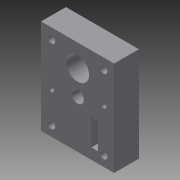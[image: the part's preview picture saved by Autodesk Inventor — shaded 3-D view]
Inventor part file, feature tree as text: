
AUTODESK INVENTOR PART (.ipt)
format: ipt  version: 2015 (Build 190159000, 159)  size: 169,984 bytes
history: native  units: mm
features: chamfer x6, hole x4, extrude x1, sketch x1
ambient origin geometry x8: Origin, YZ Plane, XZ Plane, XY Plane, X Axis, Y Axis, Z Axis, Center Point
bodies: Solid1 (feature_tree)
feature tree (12):
  extrude  "Extrusion1"  Depth=23.5mm
  hole  "Hole1"  [1 undecoded]
  hole  "Hole2"  [1 undecoded]
  hole  "Hole3"  [1 undecoded]
  hole  "Hole4"  [1 undecoded]
  chamfer  "Chamfer1"  Distance=23.5mm
  chamfer  "Chamfer2"  Distance=70.5mm
  chamfer  "Chamfer3"  Distance=21.625mm
  chamfer  "Chamfer4"  Distance=70.5mm
  chamfer  "Chamfer5"  Distance=91.5mm
  chamfer  "Chamfer6"  Distance=10.0mm
  sketch  "Sketch1"  dims[d0=21.0mm d1=23.5mm d2=10.5mm d3=11.75mm d5=23.5mm d6=5.0mm d7=23.5mm d9=70.5mm d40=21.625mm d41=70.5mm d42=91.5mm d43=10.0mm d44=10.0mm d45=7.0mm d46=10.0mm d47=10.0mm d48=90.0deg d50=7.0mm d51=10.0mm d52=10.0mm d53=7.0mm d54=10.0mm d55=10.0mm d56=7.0mm d60=30.0mm d61=30.0mm d62=5.0mm d63=5.0mm d64=14.0mm d65=24.0mm d66=0.0mm d67=10.0mm d68=10.0mm d69=3.0mm d70=6.0mm d71=10.0mm d72=7.0mm d73=90.0deg d74=8.0mm d75=20.594885mm d76=10.0mm d77=10.0mm d78=3.0mm d79=6.0mm d80=10.0mm d81=7.0mm d82=90.0deg d83=8.0mm d84=20.594885mm d85=10.0mm d86=10.0mm d87=3.0mm d88=6.0mm d89=10.0mm d90=7.0mm d91=90.0deg d92=8.0mm d93=20.594885mm d94=10.0mm d95=10.0mm d96=3.0mm d97=6.0mm d98=10.0mm d99=7.0mm d100=90.0deg d101=8.0mm d102=20.594885mm d103=0.698mm d104=20.0mm d105=0.349066mm d106=0.698mm d107=20.0mm d108=0.349066mm d109=0.698mm d110=20.0mm d111=0.349066mm d112=20.0mm d113=0.698mm d114=0.349066mm d115=0.698mm d116=20.0mm d117=0.349066mm d118=0.698mm d119=20.0mm d120=0.349066mm]
note: 4 required parameter values undecoded (feature->parameter linkage not recoverable at this tier; creation-order binding heuristic only, values carry confidence <= 0.55)
